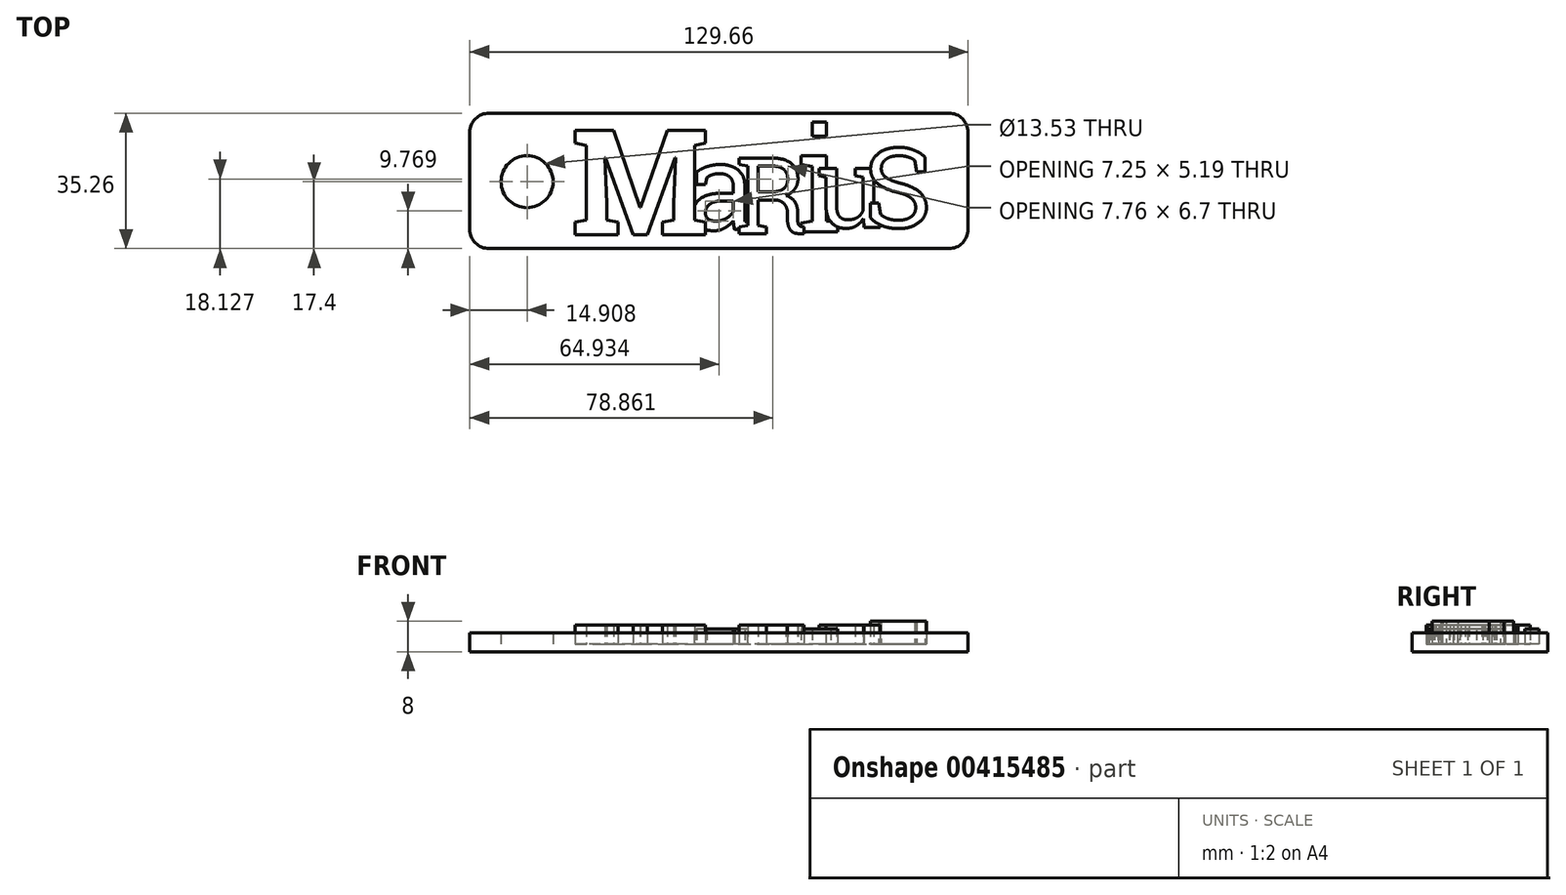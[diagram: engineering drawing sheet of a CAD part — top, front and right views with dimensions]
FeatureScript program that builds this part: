
annotation { "Feature Type Name" : "Feature", "Feature Type Description" : "" }
export const myFeature = defineFeature(function(context is Context, id is Id, definition is map)
    precondition{}
    {
        {
            var Q0;
            Q0=qCreatedBy(makeId("Top.planeOp"),FACE);
            var sketch = newSketch(context, id + "F0", { "sketchPlane" : qUnion([Q0])});
            skText(sketch, "E0", { "text": "M", "fontName": "RobotoSlab-Bold.ttf"});
            const initialGuessF0  = {"E0": [-0.04895, -0.01375, 1, 0, 0.02743], "E0": [-0.04895, -0.01375, 1, 0, 0.02743], "E0": [-0.04895, -0.01375, 1, 0, 0.02743]};
            skSetInitialGuess(sketch, initialGuessF0);
            skSolve(sketch);
        }
        {
            var Q0;
            Q0=qCreatedBy(makeId("Top.planeOp"),FACE);
            var sketch = newSketch(context, id + "F1", { "sketchPlane" : qUnion([Q0])});
            skText(sketch, "E1", { "text": "a", "fontName": "RobotoSlab-Regular.ttf"});
            const initialGuessF1  = {"E1": [-0.01864, -0.01244, 1, 0, 0.02266]};
            skSetInitialGuess(sketch, initialGuessF1);
            skSolve(sketch);
        }
        {
            var Q0;
            Q0=qCreatedBy(makeId("Top.planeOp"),FACE);
            var sketch = newSketch(context, id + "F2", { "sketchPlane" : qUnion([Q0])});
            skText(sketch, "E2", { "text": "R", "fontName": "RobotoSlab-Regular.ttf"});
            const initialGuessF2  = {"E2": [-0.00616, -0.0135, 1, 0, 0.01992]};
            skSetInitialGuess(sketch, initialGuessF2);
            skSolve(sketch);
        }
        {
            var Q0;
            Q0=qCreatedBy(makeId("Top.planeOp"),FACE);
            var sketch = newSketch(context, id + "F3", { "sketchPlane" : qUnion([Q0])});
            skText(sketch, "E3", { "text": "i", "fontName": "RobotoSlab-Regular.ttf"});
            const initialGuessF3  = {"E3": [0.00925, -0.01305, 1, 0, 0.02701]};
            skSetInitialGuess(sketch, initialGuessF3);
            skSolve(sketch);
        }
        {
            var Q0;
            Q0=qCreatedBy(makeId("Top.planeOp"),FACE);
            var sketch = newSketch(context, id + "F4", { "sketchPlane" : qUnion([Q0])});
            skText(sketch, "E4", { "text": "u", "fontName": "RobotoSlab-Regular.ttf"});
            const initialGuessF4  = {"E4": [0.01489, -0.01186, 1, 0, 0.02083]};
            skSetInitialGuess(sketch, initialGuessF4);
            skSolve(sketch);
        }
        {
            var Q0;
            Q0=qCreatedBy(makeId("Top.planeOp"),FACE);
            var sketch = newSketch(context, id + "F5", { "sketchPlane" : qUnion([Q0])});
            skText(sketch, "E5", { "text": "S", "fontName": "RobotoSlab-Regular.ttf"});
            const initialGuessF5  = {"E5": [0.02724, -0.0119, 1, 0, 0.02083]};
            skSetInitialGuess(sketch, initialGuessF5);
            skSolve(sketch);
        }
        {
            var Q0;
            Q0 = qSketchRegion(id + "F0", true);
            extrude(context, id + "F6", {"entities" : qUnion([Q0]), "depth" : 5 * mm, "offsetDistance" : 25 * mm});
        }
        {
            var Q0;
            Q0 = qSketchRegion(id + "F1", true);
            extrude(context, id + "F7", {"entities" : qUnion([Q0]), "operationType" : NewBodyOperationType.ADD, "depth" : 4 * mm, "offsetDistance" : 25 * mm});
        }
        {
            var Q0;
            Q0 = qSketchRegion(id + "F2", true);
            extrude(context, id + "F8", {"entities" : qUnion([Q0]), "operationType" : NewBodyOperationType.ADD, "depth" : 5 * mm, "offsetDistance" : 25 * mm});
        }
        {
            var Q0;
            Q0 = qSketchRegion(id + "F3", true);
            extrude(context, id + "F9", {"entities" : qUnion([Q0]), "operationType" : NewBodyOperationType.ADD, "depth" : 4 * mm, "offsetDistance" : 25 * mm});
        }
        {
            var Q0;
            Q0 = qSketchRegion(id + "F4", true);
            extrude(context, id + "F10", {"entities" : qUnion([Q0]), "operationType" : NewBodyOperationType.ADD, "depth" : 5 * mm, "offsetDistance" : 25 * mm});
        }
        {
            var Q0;
            Q0 = qSketchRegion(id + "F5", true);
            extrude(context, id + "F11", {"entities" : qUnion([Q0]), "operationType" : NewBodyOperationType.ADD, "depth" : 6 * mm, "offsetDistance" : 25 * mm});
        }
        {
            var Q0;
            Q0=qCreatedBy(makeId("Top.planeOp"),FACE);
            var sketch = newSketch(context, id + "F12", { "sketchPlane" : qUnion([Q0])});
            skLineSegment(sketch, "E6.bottom", {"start": v(-70.32, 17.86) * mm, "end": v(49.34, 17.86) * mm});
            skLineSegment(sketch, "E6.top", {"start": v(-70.32, -17.4) * mm, "end": v(49.34, -17.4) * mm});
            skLineSegment(sketch, "E6.left", {"start": v(-75.32, 12.86) * mm, "end": v(-75.32, -12.4) * mm});
            skLineSegment(sketch, "E6.right", {"start": v(54.34, 12.86) * mm, "end": v(54.34, -12.4) * mm});
            skPoint(sketch, "E7.visualSharp", {"position": v(54.34, 17.86) * mm});
            skArc(sketch, "E7.filletArc", {"start": v(54.34, 12.86) * mm, "mid": v(52.87, 16.4) * mm, "end": v(49.34, 17.86) * mm});
            skPoint(sketch, "E8.visualSharp", {"position": v(54.34, -17.4) * mm});
            skArc(sketch, "E8.filletArc", {"start": v(49.34, -17.4) * mm, "mid": v(52.87, -15.93) * mm, "end": v(54.34, -12.4) * mm});
            skPoint(sketch, "E9.visualSharp", {"position": v(-75.32, -17.4) * mm});
            skArc(sketch, "E9.filletArc", {"start": v(-75.32, -12.4) * mm, "mid": v(-73.85, -15.93) * mm, "end": v(-70.32, -17.4) * mm});
            skPoint(sketch, "E10.visualSharp", {"position": v(-75.32, 17.86) * mm});
            skArc(sketch, "E10.filletArc", {"start": v(-70.32, 17.86) * mm, "mid": v(-73.85, 16.4) * mm, "end": v(-75.32, 12.86) * mm});
            skCircle(sketch, "E11", {"center": v(-60.41, 0) * mm, "radius": 6.76 * mm});
            skSolve(sketch);
        }
        {
            var Q0;
            Q0=makeQuery(id+"F12.imprint","IMPRINT",FACE,{"disambiguationData":[TD([[makeQuery(id+"F12.imprint","IMPRINT",EDGE,{"derivedFrom":sQuery(id+"F12.wireOp",EDGE,"E6.bottom")}),-1.0]])]});
            extrude(context, id + "F13", {"entities" : qUnion([Q0]), "depth" : 5 * mm, "offsetDistance" : 25 * mm});
        }
        {
            var Q0;
            Q0=makeQuery(id+"F13.opExtrude","SWEPT_BODY",BODY,{"disambiguationData":[OSD([sQuery(id+"F12.wireOp",EDGE,"E6.bottom"),sQuery(id+"F12.wireOp",EDGE,"E6.top"),sQuery(id+"F12.wireOp",EDGE,"E6.left"),sQuery(id+"F12.wireOp",EDGE,"E6.right"),sQuery(id+"F12.wireOp",EDGE,"E7.filletArc"),sQuery(id+"F12.wireOp",EDGE,"E8.filletArc"),sQuery(id+"F12.wireOp",EDGE,"E9.filletArc"),sQuery(id+"F12.wireOp",EDGE,"E10.filletArc"),sQuery(id+"F12.wireOp",EDGE,"E11")])]});
            transform(context, id + "F14", {"entities" : qUnion([Q0]), "transformType" : TransformType.TRANSLATION_3D, "dx" : 0 * mm, "dy" : 0 * mm, "dz" : -2 * mm, "makeCopy" : false});
        }
    });
